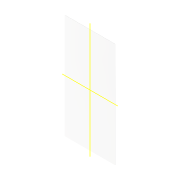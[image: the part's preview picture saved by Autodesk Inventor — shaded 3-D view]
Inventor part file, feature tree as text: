
AUTODESK INVENTOR PART (.ipt)
format: ipt  version: 2022 (Build 260153000, 153)  size: 79,360 bytes
history: native  units: mm
features: plane x2, extrude x1, sketch x1
ambient origin geometry x8: Origin, YZ Plane, XZ Plane, XY Plane, X Axis, Y Axis, Z Axis, Center Point
bodies: Solid1 (feature_tree)
feature tree (4):
  extrude  "Extrusion1"  Depth=50.0mm
  plane  "Work Plane1"
  plane  "Work Plane2"
  sketch  "Sketch1"  dims[d0=24.0mm d1=50.0mm d2=0.125mm d3=0.0mm]
